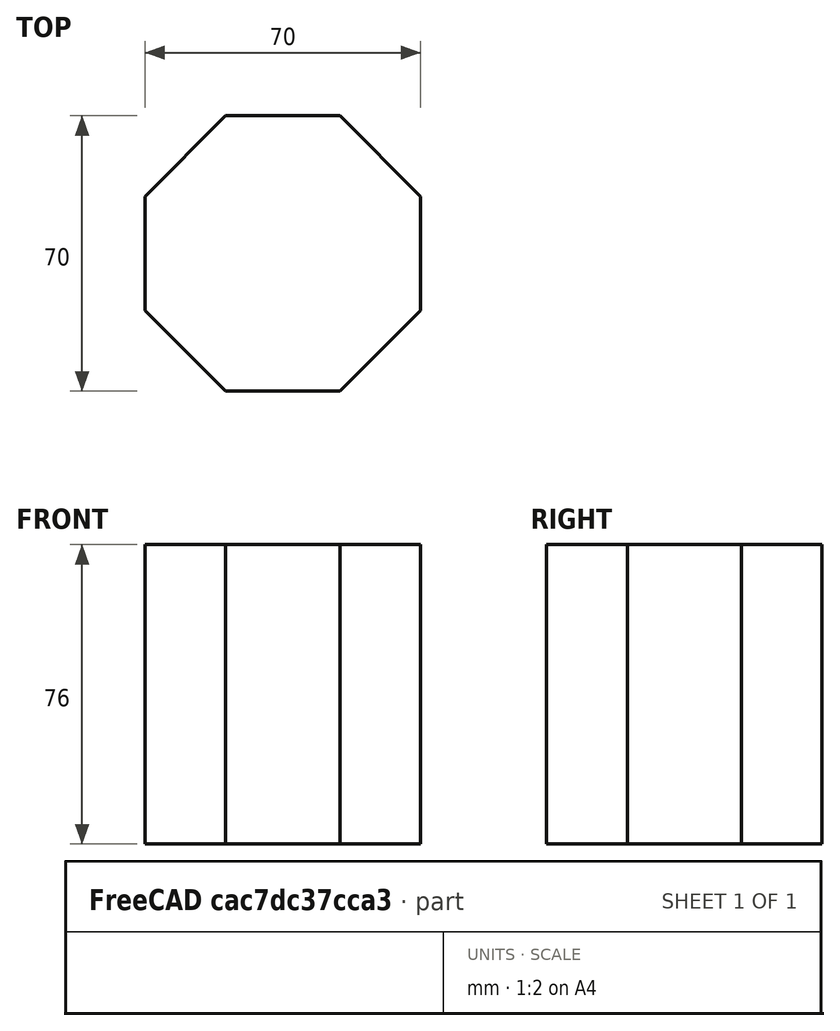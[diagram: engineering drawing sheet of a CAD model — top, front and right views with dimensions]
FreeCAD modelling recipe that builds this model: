
FCSTD DOCUMENT  (FreeCAD 1.0R39319 (Git))
Label: OCT-CHBAS-AA
License: All rights reserved
LicenseURL: https://en.wikipedia.org/wiki/All_rights_reserved
objects: App::Link×1, Sketcher::SketchObject×1, PartDesign::Pad×1, PartDesign::CoordinateSystem×1, PartDesign::Body×1
note: 7 computed .brp shape members not serialized (recipe doc carries the construction recipe); baked Part::Feature solids carry a one-line shape summary decoded from their .brp
EXTERNAL_REF file=../master.FCStd obj=Spreadsheet

FEATURE [App::Link] Link  label="dims"
  LinkedObject = -> <external ../master.FCStd>#Spreadsheet
FEATURE [Sketcher::SketchObject] Sketch
  ArcFitTolerance = 1e-06
  AttachmentSupport = -> [XY_Plane]
  FullyConstrained = true
  MakeInternals = false
  MapMode = 5
  expr: Constraints[25] = <<dims>>.iwChamber
  sketch-geometry (9):
    g0: LineSegment StartX=-35 StartY=14.4975 StartZ=0 EndX=-35 EndY=-14.4975 EndZ=0
    g1: LineSegment StartX=-35 StartY=-14.4975 StartZ=0 EndX=-14.4975 EndY=-35 EndZ=0
    g2: LineSegment StartX=-14.4975 StartY=-35 StartZ=0 EndX=14.4975 EndY=-35 EndZ=0
    g3: LineSegment StartX=14.4975 StartY=-35 StartZ=0 EndX=35 EndY=-14.4975 EndZ=0
    g4: LineSegment StartX=35 StartY=-14.4975 StartZ=0 EndX=35 EndY=14.4975 EndZ=0
    g5: LineSegment StartX=35 StartY=14.4975 StartZ=0 EndX=14.4975 EndY=35 EndZ=0
    g6: LineSegment StartX=14.4975 StartY=35 StartZ=0 EndX=-14.4975 EndY=35 EndZ=0
    g7: LineSegment StartX=-14.4975 StartY=35 StartZ=0 EndX=-35 EndY=14.4975 EndZ=0
    g8: Circle [constr] CenterX=0 CenterY=0 CenterZ=0 NormalX=0 NormalY=0 NormalZ=1 AngleXU=0 Radius=37.8837
  constraints (20):
    c: Coincident(g0,g1)
    c: Coincident(g1,g2)
    c: Coincident(g2,g3)
    c: Coincident(g3,g4)
    c: Coincident(g4,g5)
    c: Coincident(g5,g6)
    c: Coincident(g6,g7)
    c: Coincident(g7,g0)
    c: Equal(g0, g1-g7) x7
    c: PointOnObject(g0,g8)
    c: PointOnObject(g1,g8)
    c: PointOnObject(g2,g8)
    c: PointOnObject(g3,g8)
    c: PointOnObject(g4,g8)
    c: PointOnObject(g5,g8)
    c: PointOnObject(g6,g8)
    c: PointOnObject(g7,g8)
    c: Coincident(g8,g-1)
    c: Horizontal(g6)
    c: DistanceY(g1,g6) = 70
FEATURE [PartDesign::Pad] Pad
  Direction = (0,0,1)
  Length = 76
  Length2 = 10
  Profile = -> Sketch
  ReferenceAxis = -> Sketch [N_Axis]
  Refine = true
  Suppressed = false
  Type = 0
  expr: Length = <<dims>>.tcBase
FEATURE [PartDesign::CoordinateSystem] Local_CS
  AttacherType = Attacher::AttachEngine3D
  MapMode = 2
FEATURE [PartDesign::Body] Body  label="base"
  AllowCompound = false
  Group = -> [Sketch,Pad,Local_CS]
  Origin = -> Origin
  Tip = -> Pad
